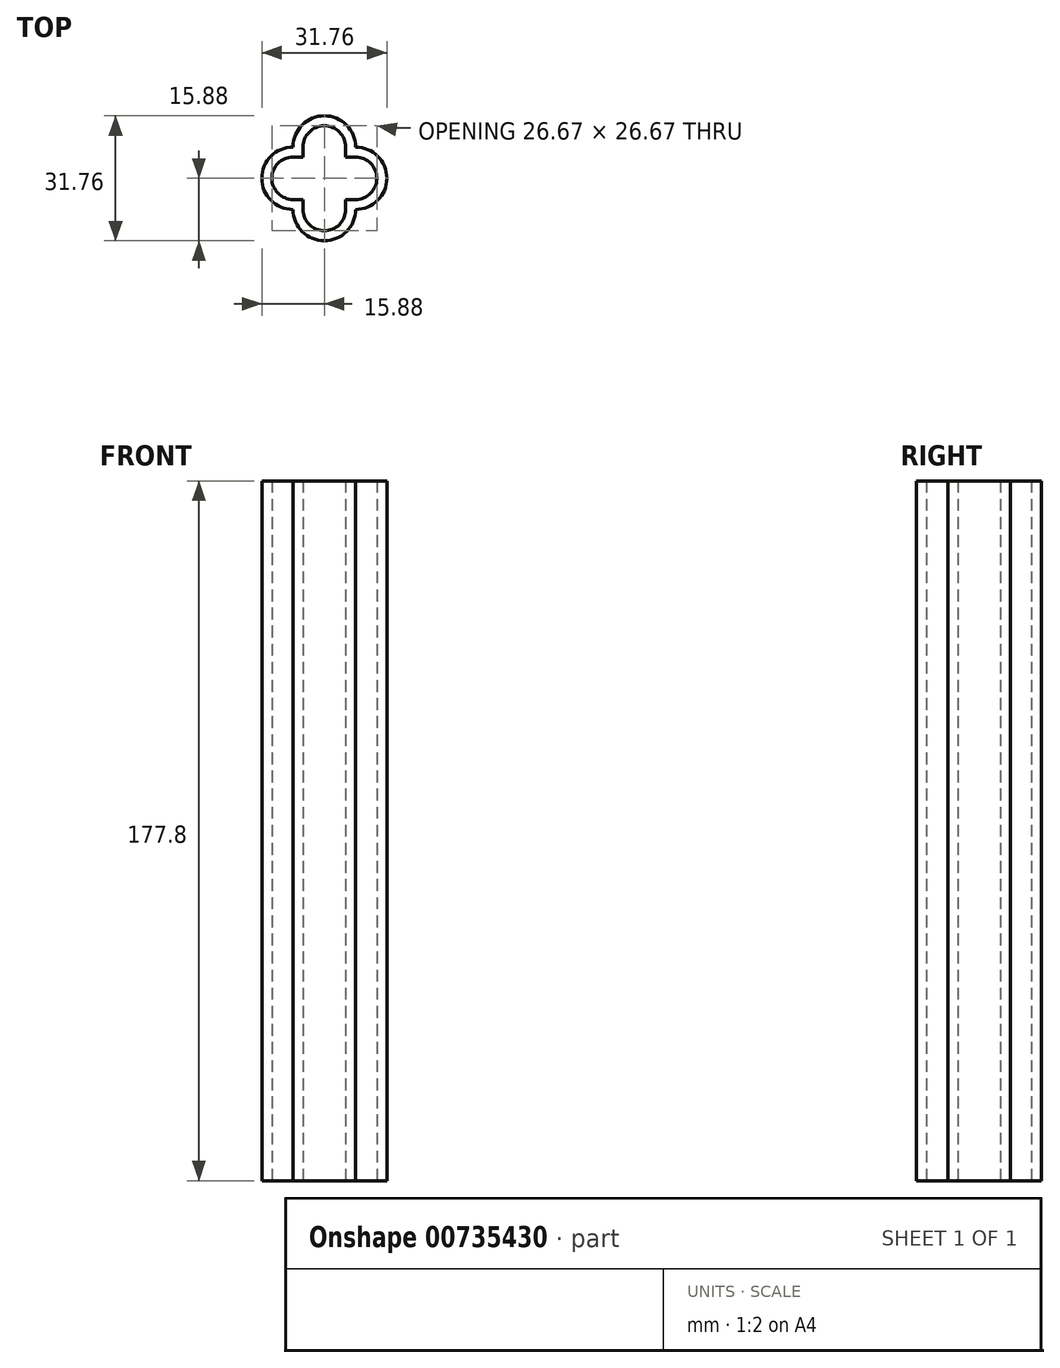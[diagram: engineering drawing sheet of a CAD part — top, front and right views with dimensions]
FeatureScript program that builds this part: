
annotation { "Feature Type Name" : "Feature", "Feature Type Description" : "" }
export const myFeature = defineFeature(function(context is Context, id is Id, definition is map)
    precondition{}
    {
        {
            var Q0;
            Q0=qCreatedBy(makeId("Top.planeOp"),FACE);
            var sketch = newSketch(context, id + "F0", { "sketchPlane" : qUnion([Q0])});
            skLineSegment(sketch, "E0.bottom", {"start": v(-7.94, 7.94) * mm, "end": v(7.94, 7.94) * mm});
            skLineSegment(sketch, "E0.top", {"start": v(-7.94, -7.94) * mm, "end": v(7.94, -7.94) * mm});
            skLineSegment(sketch, "E0.left", {"start": v(-7.94, 7.94) * mm, "end": v(-7.94, -7.94) * mm});
            skLineSegment(sketch, "E0.right", {"start": v(7.94, 7.94) * mm, "end": v(7.94, -7.94) * mm});
            skPoint(sketch, "E0.middle", {"position": v(0, 0) * mm});
            skArc(sketch, "E1", {"start": v(7.94, 7.94) * mm, "mid": v(0, 15.88) * mm, "end": v(-7.94, 7.94) * mm});
            skArc(sketch, "E2", {"start": v(7.94, -7.94) * mm, "mid": v(15.88, 0) * mm, "end": v(7.94, 7.94) * mm});
            skArc(sketch, "E3", {"start": v(-7.94, -7.94) * mm, "mid": v(0, -15.88) * mm, "end": v(7.94, -7.94) * mm});
            skArc(sketch, "E4", {"start": v(-7.94, 7.94) * mm, "mid": v(-15.88, 0) * mm, "end": v(-7.94, -7.94) * mm});
            skArc(sketch, "E5.0", {"start": v(-7.94, 5.4) * mm, "mid": v(-13.34, 0) * mm, "end": v(-7.94, -5.4) * mm});
            skArc(sketch, "E6.0", {"start": v(5.4, 7.94) * mm, "mid": v(0, 13.34) * mm, "end": v(-5.4, 7.94) * mm});
            skArc(sketch, "E7.0", {"start": v(7.94, -5.4) * mm, "mid": v(13.34, 0) * mm, "end": v(7.94, 5.4) * mm});
            skArc(sketch, "E8.0", {"start": v(-5.4, -7.94) * mm, "mid": v(0, -13.33) * mm, "end": v(5.4, -7.94) * mm});
            skLineSegment(sketch, "E9", {"start": v(-5.4, 7.94) * mm, "end": v(-5.4, -7.94) * mm});
            skLineSegment(sketch, "E10", {"start": v(5.4, -7.94) * mm, "end": v(5.4, 7.94) * mm});
            skLineSegment(sketch, "E11", {"start": v(-7.94, 5.4) * mm, "end": v(7.94, 5.4) * mm});
            skLineSegment(sketch, "E12", {"start": v(-7.94, -5.4) * mm, "end": v(7.94, -5.4) * mm});
            skSolve(sketch);
        }
        {
            var Q0;
            {var subQ3=sQuery(id+"F0.wireOp",EDGE,"E9");var subQ5=sQuery(id+"F0.wireOp",EDGE,"E11");var subQ6=makeQuery(id+"F0.imprint","INTERSECT",VERTEX,{"derivedFrom":[subQ3,subQ5]});Q0=makeQuery(id+"F0.imprint","IMPRINT",FACE,{"disambiguationData":[TD([[makeQuery(id+"F0.imprint","IMPRINT",EDGE,{"disambiguationData":[TD([[subQ6,1.0]])],"derivedFrom":subQ3}),-1.0]])]});}
            var Q1;
            {var subQ3=sQuery(id+"F0.wireOp",EDGE,"E10");var subQ5=sQuery(id+"F0.wireOp",EDGE,"E11");var subQ7=makeQuery(id+"F0.imprint","INTERSECT",VERTEX,{"derivedFrom":[subQ3,subQ5]});Q1=makeQuery(id+"F0.imprint","IMPRINT",FACE,{"disambiguationData":[TD([[makeQuery(id+"F0.imprint","IMPRINT",EDGE,{"disambiguationData":[TD([[subQ7,-1.0]])],"derivedFrom":subQ3}),-1.0]])]});}
            var Q2;
            {var subQ0=sQuery(id+"F0.wireOp",EDGE,"E1");Q2=makeQuery(id+"F0.imprint","IMPRINT",FACE,{"disambiguationData":[TD([[makeQuery(id+"F0.imprint","IMPRINT",EDGE,{"derivedFrom":subQ0}),1.0]])]});}
            var Q3;
            {var subQ0=sQuery(id+"F0.wireOp",EDGE,"E3");Q3=makeQuery(id+"F0.imprint","IMPRINT",FACE,{"disambiguationData":[TD([[makeQuery(id+"F0.imprint","IMPRINT",EDGE,{"derivedFrom":subQ0}),1.0]])]});}
            var Q4;
            {var subQ0=sQuery(id+"F0.wireOp",EDGE,"E4");Q4=makeQuery(id+"F0.imprint","IMPRINT",FACE,{"disambiguationData":[TD([[makeQuery(id+"F0.imprint","IMPRINT",EDGE,{"derivedFrom":subQ0}),1.0]])]});}
            var Q5;
            {var subQ0=sQuery(id+"F0.wireOp",EDGE,"E2");Q5=makeQuery(id+"F0.imprint","IMPRINT",FACE,{"disambiguationData":[TD([[makeQuery(id+"F0.imprint","IMPRINT",EDGE,{"derivedFrom":subQ0}),1.0]])]});}
            var Q6;
            {var subQ3=sQuery(id+"F0.wireOp",EDGE,"E9");var subQ5=sQuery(id+"F0.wireOp",EDGE,"E12");var subQ7=makeQuery(id+"F0.imprint","INTERSECT",VERTEX,{"derivedFrom":[subQ3,subQ5]});Q6=makeQuery(id+"F0.imprint","IMPRINT",FACE,{"disambiguationData":[TD([[makeQuery(id+"F0.imprint","IMPRINT",EDGE,{"disambiguationData":[TD([[subQ7,-1.0]])],"derivedFrom":subQ3}),-1.0]])]});}
            var Q7;
            {var subQ3=sQuery(id+"F0.wireOp",EDGE,"E10");var subQ5=sQuery(id+"F0.wireOp",EDGE,"E12");var subQ7=makeQuery(id+"F0.imprint","INTERSECT",VERTEX,{"derivedFrom":[subQ3,subQ5]});Q7=makeQuery(id+"F0.imprint","IMPRINT",FACE,{"disambiguationData":[TD([[makeQuery(id+"F0.imprint","IMPRINT",EDGE,{"disambiguationData":[TD([[subQ7,1.0]])],"derivedFrom":subQ3}),-1.0]])]});}
            extrude(context, id + "F1", {"entities" : qUnion([Q0, Q1, Q2, Q3, Q4, Q5, Q6, Q7]), "depth" : 177.8 * mm, "offsetDistance" : 25.4 * mm});
        }
    });
